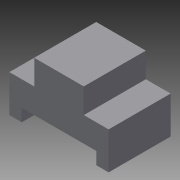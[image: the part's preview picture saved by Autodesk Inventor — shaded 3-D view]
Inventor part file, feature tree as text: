
AUTODESK INVENTOR PART (.ipt)
format: ipt  version: 2015 (Build 190159000, 159)  size: 76,800 bytes
history: native  units: in
note: dims shown in document units (in); Inventor stores cm internally (conversion verified against a paired STEP export)
features: extrude x1, sketch x1
ambient origin geometry x8: Origin, YZ Plane, XZ Plane, XY Plane, X Axis, Y Axis, Z Axis, Center Point
bodies: Solid1 (feature_tree)
feature tree (2):
  extrude  "Extrusion1"  [1 undecoded]
  sketch  "Sketch1"  dims[d7=1.25in d8=0.0in]
note: 1 required parameter value undecoded (feature->parameter linkage not recoverable at this tier; creation-order binding heuristic only, values carry confidence <= 0.55)
